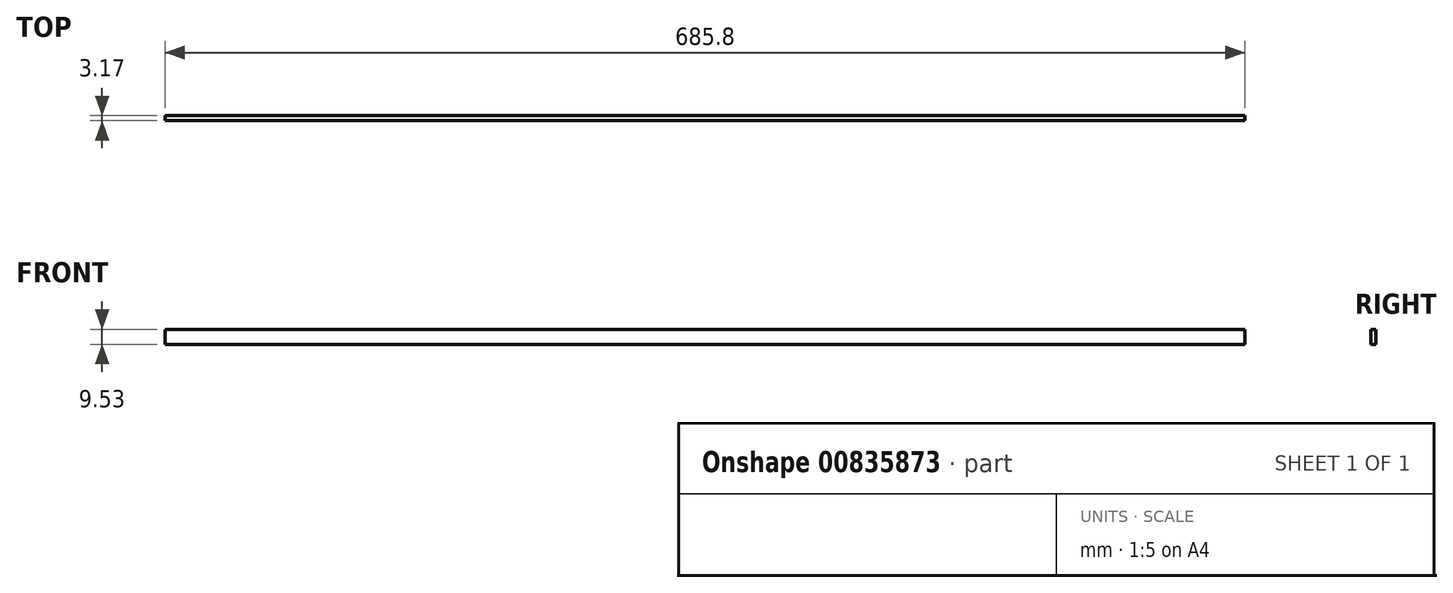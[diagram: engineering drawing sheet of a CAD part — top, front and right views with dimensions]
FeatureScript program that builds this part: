
annotation { "Feature Type Name" : "Feature", "Feature Type Description" : "" }
export const myFeature = defineFeature(function(context is Context, id is Id, definition is map)
    precondition{}
    {
        {
            var Q0;
            Q0=qCreatedBy(makeId("Right.planeOp"),FACE);
            var sketch = newSketch(context, id + "F0", { "sketchPlane" : qUnion([Q0])});
            skLineSegment(sketch, "E0.bottom", {"start": v(0, 0) * mm, "end": v(3.18, 0) * mm});
            skLineSegment(sketch, "E0.top", {"start": v(0, 9.52) * mm, "end": v(3.18, 9.52) * mm});
            skLineSegment(sketch, "E0.left", {"start": v(0, 0) * mm, "end": v(0, 9.52) * mm});
            skLineSegment(sketch, "E0.right", {"start": v(3.18, 0) * mm, "end": v(3.18, 9.52) * mm});
            skSolve(sketch);
        }
        {
            var Q0;
            Q0=qSketchRegion(id+"F0",true);
            extrude(context, id + "F1", {"entities" : qUnion([Q0]), "depth" : 685.8 * mm, "offsetDistance" : 25.4 * mm});
        }
    });
